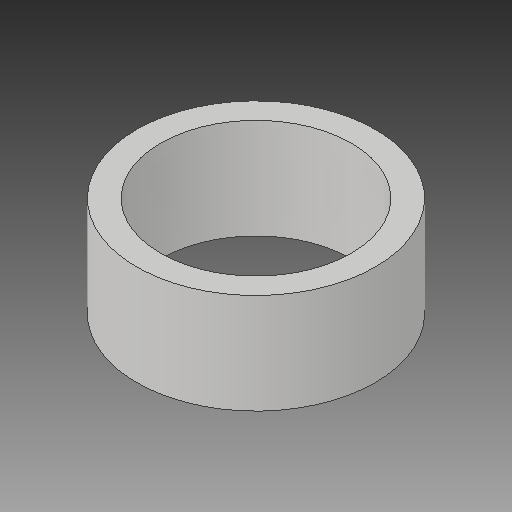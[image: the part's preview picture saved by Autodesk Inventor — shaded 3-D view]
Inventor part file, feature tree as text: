
AUTODESK INVENTOR PART (.ipt)
format: ipt  version: 2018.3 (Build 223284000, 284)  size: 87,552 bytes
history: native  units: mm
features: other x1, extrude x1, sketch x1
ambient origin geometry x8: Origin, YZ Plane, XZ Plane, XY Plane, X Axis, Y Axis, Z Axis, Center Point
bodies: Body1 (feature_tree)
feature tree (3):
  other  "ソリッド1"
  extrude  "押し出し1"  Depth=10.0mm
  sketch  "スケッチ1"
